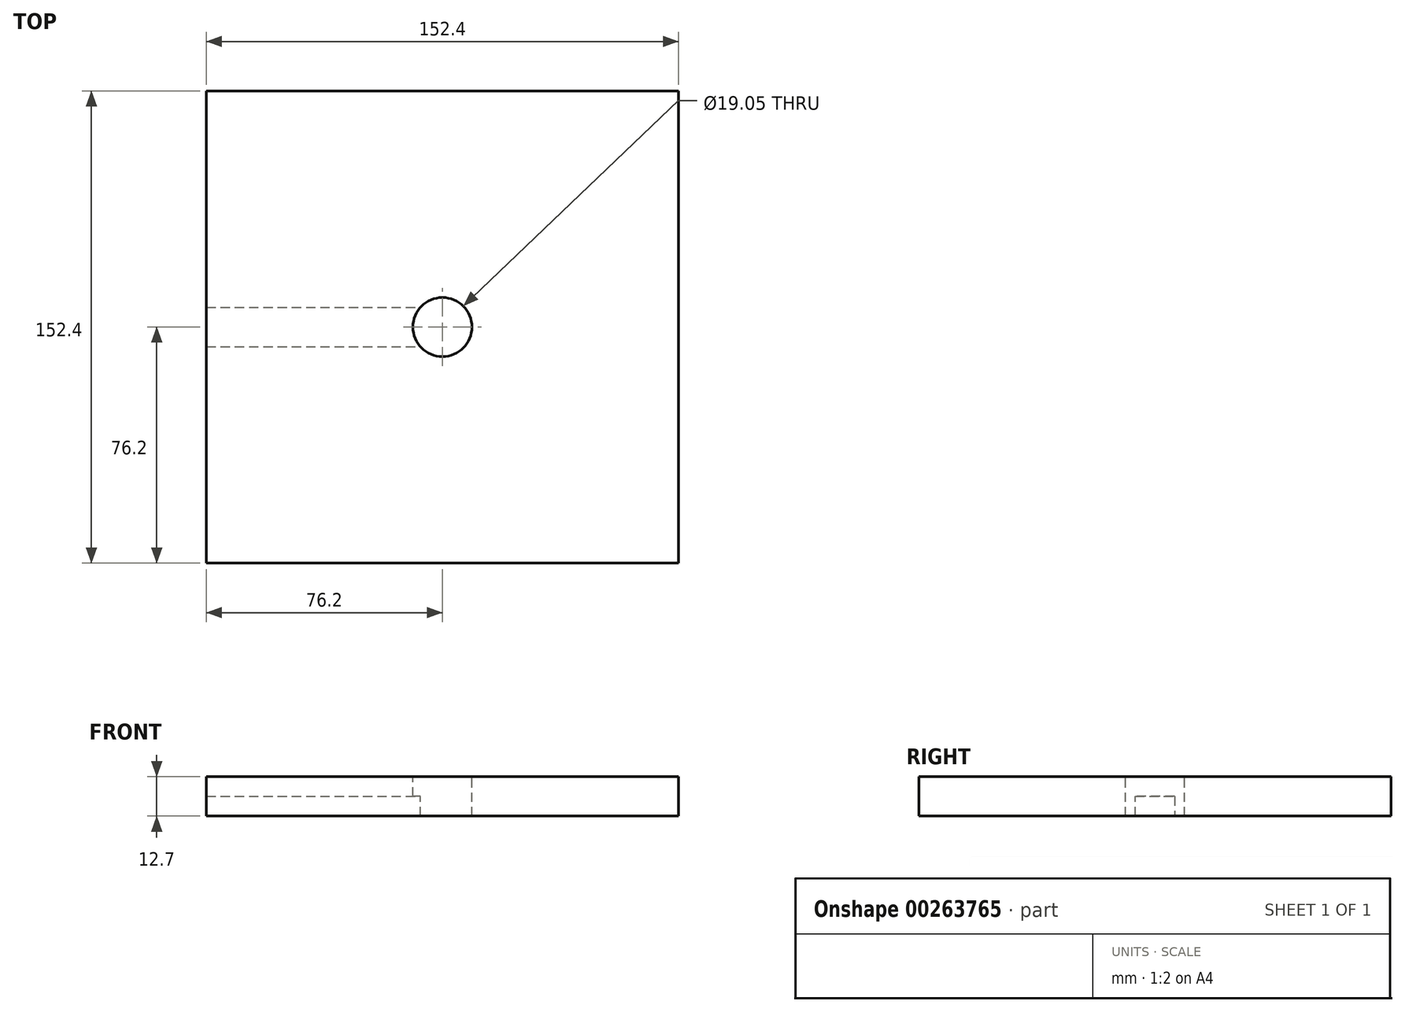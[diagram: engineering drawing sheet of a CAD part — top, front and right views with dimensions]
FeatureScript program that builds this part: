
annotation { "Feature Type Name" : "Feature", "Feature Type Description" : "" }
export const myFeature = defineFeature(function(context is Context, id is Id, definition is map)
    precondition{}
    {
        {
            var Q0;
            Q0=qCreatedBy(makeId("Top.planeOp"),FACE);
            var sketch = newSketch(context, id + "F0", { "sketchPlane" : qUnion([Q0])});
            skLineSegment(sketch, "E0.bottom", {"start": v(-76.2, 76.2) * mm, "end": v(76.2, 76.2) * mm});
            skLineSegment(sketch, "E0.top", {"start": v(-76.2, -76.2) * mm, "end": v(76.2, -76.2) * mm});
            skLineSegment(sketch, "E0.left", {"start": v(-76.2, 76.2) * mm, "end": v(-76.2, -76.2) * mm});
            skLineSegment(sketch, "E0.right", {"start": v(76.2, 76.2) * mm, "end": v(76.2, -76.2) * mm});
            skPoint(sketch, "E0.middle", {"position": v(0, 0) * mm});
            skCircle(sketch, "E1", {"center": v(0, 0) * mm, "radius": 9.53 * mm});
            skSolve(sketch);
        }
        {
            var Q0;
            Q0=makeQuery(id+"F0.imprint","IMPRINT",FACE,{"disambiguationData":[TD([[makeQuery(id+"F0.imprint","IMPRINT",EDGE,{"derivedFrom":sQuery(id+"F0.wireOp",EDGE,"E0.bottom")}),-1.0]])]});
            extrude(context, id + "F1", {"entities" : qUnion([Q0]), "oppositeDirection" : true, "depth" : 12.7 * mm});
        }
        {
            var Q0;
            Q0=qCreatedBy(makeId("Right.planeOp"),FACE);
            var sketch = newSketch(context, id + "F2", { "sketchPlane" : qUnion([Q0])});
            skLineSegment(sketch, "E2.0", {"start": v(6.35, -12.7) * mm, "end": v(-6.35, -12.7) * mm});
            skLineSegment(sketch, "E3", {"start": v(6.35, -12.7) * mm, "end": v(6.35, -6.35) * mm});
            skLineSegment(sketch, "E4", {"start": v(6.35, -6.35) * mm, "end": v(-6.35, -6.35) * mm});
            skLineSegment(sketch, "E5", {"start": v(-6.35, -6.35) * mm, "end": v(-6.35, -12.7) * mm});
            skPoint(sketch, "E6.orphan", {"position": v(76.2, -12.7) * mm});
            skPoint(sketch, "E7.orphan", {"position": v(-76.2, -12.7) * mm});
            skSolve(sketch);
        }
        {
            var Q0;
            Q0=makeQuery(id+"F2.imprint","IMPRINT",FACE,{"disambiguationData":[TD([[makeQuery(id+"F2.imprint","IMPRINT",EDGE,{"derivedFrom":sQuery(id+"F2.wireOp",EDGE,"E2.0")}),-1.0]])]});
            extrude(context, id + "F3", {"entities" : qUnion([Q0]), "operationType" : NewBodyOperationType.REMOVE, "endBound" : BoundingType.THROUGH_ALL, "oppositeDirection" : true, "depth" : 25.4 * mm});
        }
    });
